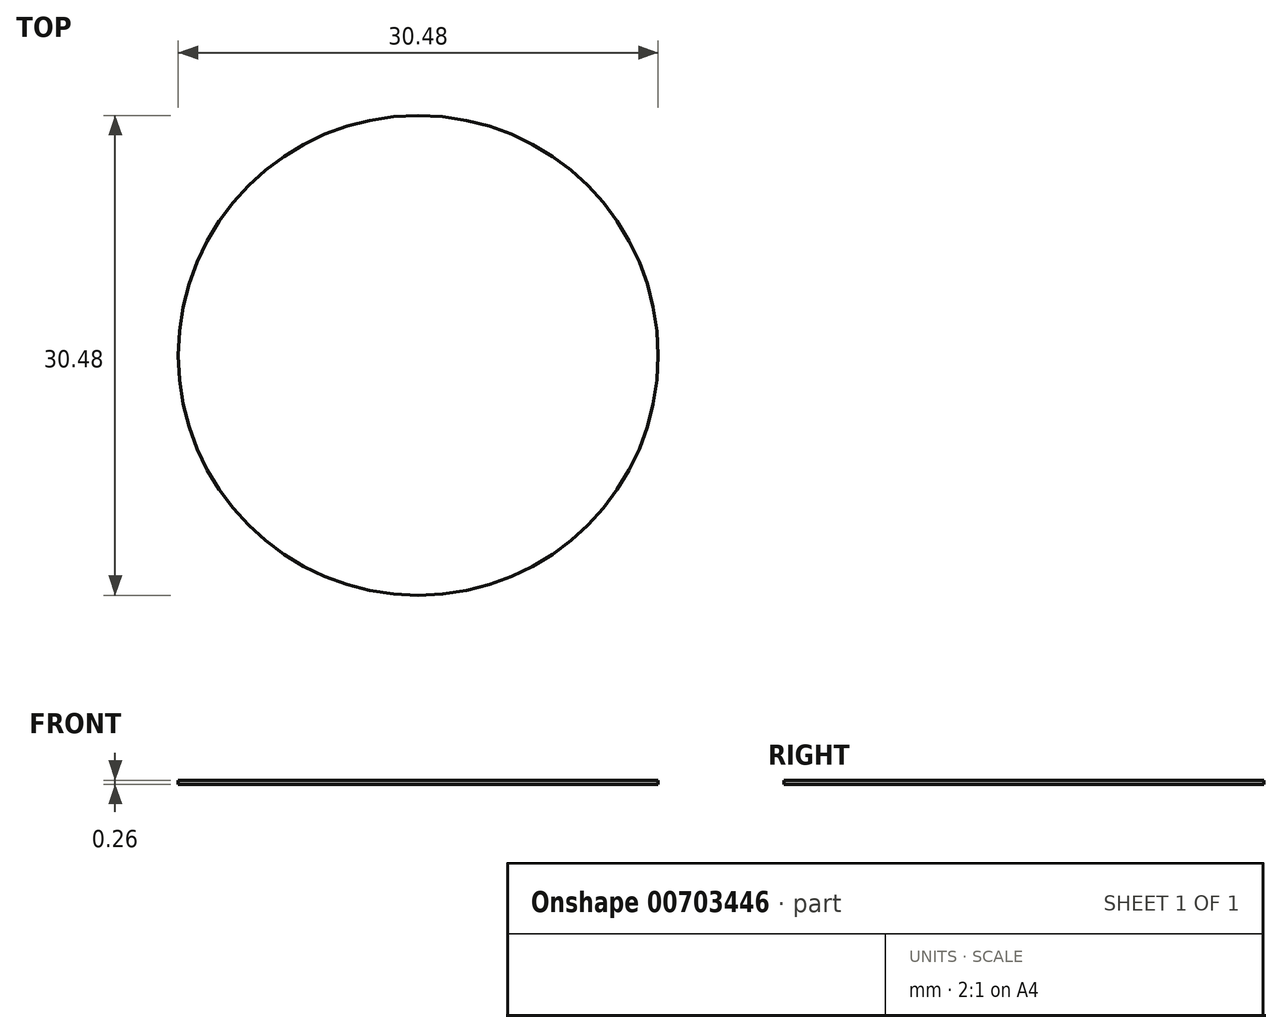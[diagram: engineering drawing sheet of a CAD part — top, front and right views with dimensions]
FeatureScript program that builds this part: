
annotation { "Feature Type Name" : "Feature", "Feature Type Description" : "" }
export const myFeature = defineFeature(function(context is Context, id is Id, definition is map)
    precondition{}
    {
        {
            var Q0;
            Q0=qCreatedBy(makeId("Top.planeOp"),FACE);
            var sketch = newSketch(context, id + "F0", { "sketchPlane" : qUnion([Q0])});
            skCircle(sketch, "E0", {"center": v(0, 0) * mm, "radius": 15.24 * mm});
            skSolve(sketch);
        }
        {
            var Q0;
            Q0=qSketchRegion(id+"F0",true);
            extrude(context, id + "F1", {"entities" : qUnion([Q0]), "endBound" : BoundingType.SYMMETRIC, "depth" : 0.25 * mm, "offsetDistance" : 25.4 * mm});
        }
    });
